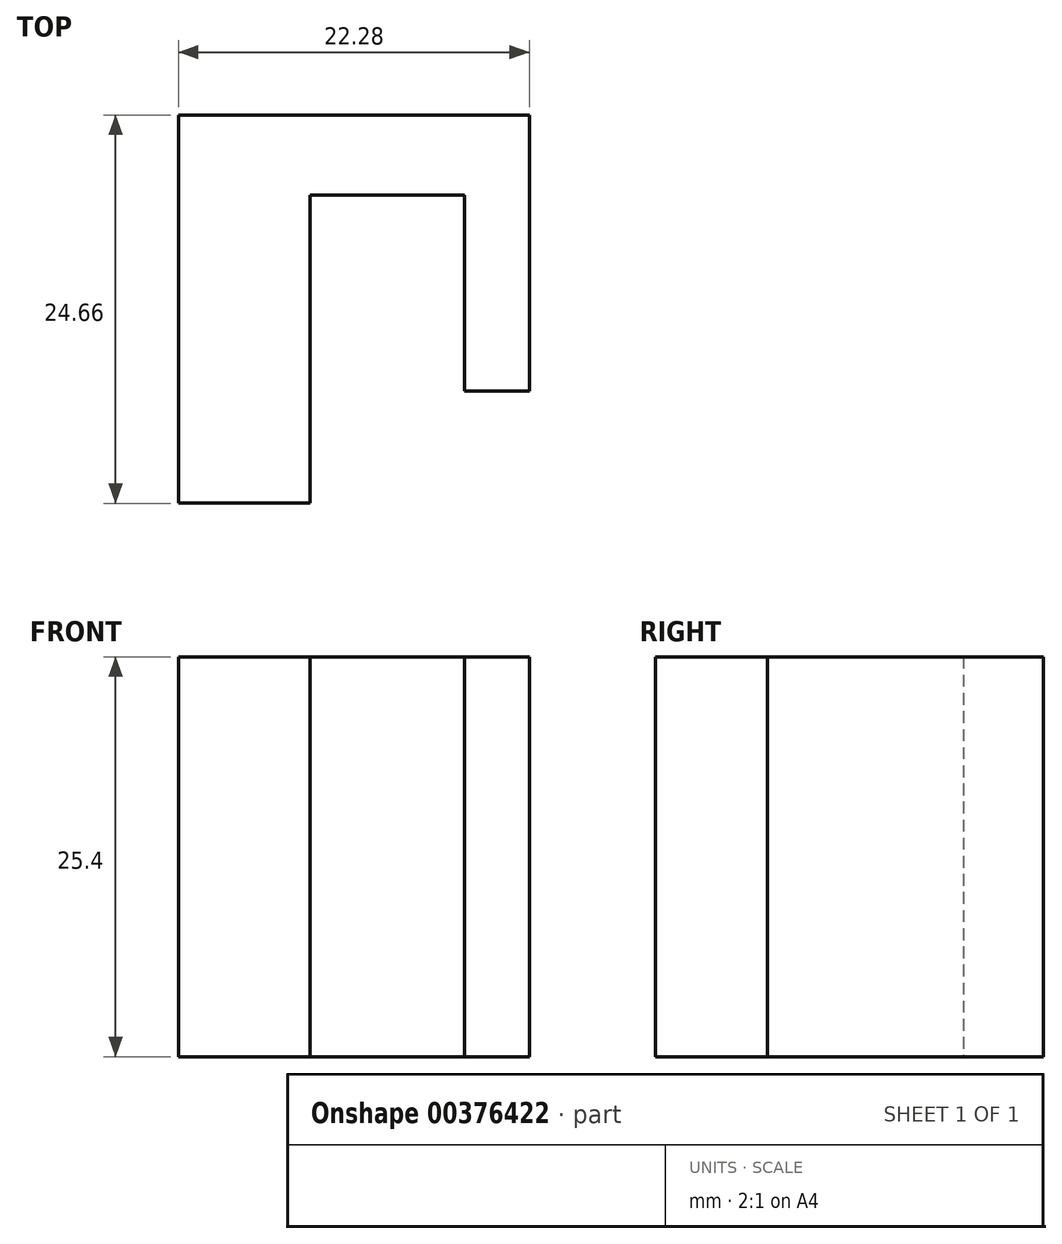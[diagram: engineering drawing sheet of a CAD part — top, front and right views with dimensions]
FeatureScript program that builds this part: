
annotation { "Feature Type Name" : "Feature", "Feature Type Description" : "" }
export const myFeature = defineFeature(function(context is Context, id is Id, definition is map)
    precondition{}
    {
        {
            var Q0;
            Q0=qCreatedBy(makeId("Top.planeOp"),FACE);
            var sketch = newSketch(context, id + "F0", { "sketchPlane" : qUnion([Q0])});
            skLineSegment(sketch, "E0.bottom", {"start": v(4.17, -12.33) * mm, "end": v(-4.17, -12.33) * mm});
            skLineSegment(sketch, "E0.top", {"start": v(4.17, 12.33) * mm, "end": v(-4.17, 12.33) * mm});
            skLineSegment(sketch, "E0.left", {"start": v(4.17, -12.33) * mm, "end": v(4.17, 12.33) * mm});
            skLineSegment(sketch, "E0.right", {"start": v(-4.17, -12.33) * mm, "end": v(-4.17, 12.33) * mm});
            skPoint(sketch, "E0.middle", {"position": v(0, 0) * mm});
            skLineSegment(sketch, "E1.bottom", {"start": v(4.17, 12.33) * mm, "end": v(18.11, 12.33) * mm});
            skLineSegment(sketch, "E1.top", {"start": v(4.17, 7.23) * mm, "end": v(18.11, 7.23) * mm});
            skLineSegment(sketch, "E1.left", {"start": v(4.17, 12.33) * mm, "end": v(4.17, 7.23) * mm});
            skLineSegment(sketch, "E1.right", {"start": v(18.11, 12.33) * mm, "end": v(18.11, 7.23) * mm});
            skLineSegment(sketch, "E2.bottom", {"start": v(18.11, 7.23) * mm, "end": v(13.99, 7.23) * mm});
            skLineSegment(sketch, "E2.top", {"start": v(18.11, -5.2) * mm, "end": v(13.99, -5.2) * mm});
            skLineSegment(sketch, "E2.left", {"start": v(18.11, 7.23) * mm, "end": v(18.11, -5.2) * mm});
            skLineSegment(sketch, "E2.right", {"start": v(13.99, 7.23) * mm, "end": v(13.99, -5.2) * mm});
            skSolve(sketch);
        }
        {
            var Q0;
            Q0 = qSketchRegion(id + "F0", true);
            extrude(context, id + "F1", {"entities" : qUnion([Q0]), "depth" : 25.4 * mm});
        }
    });
